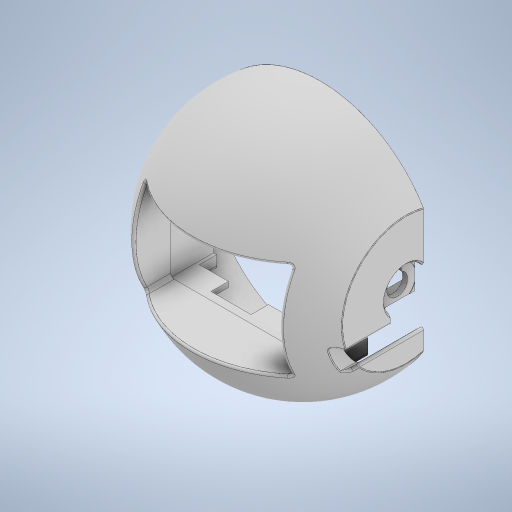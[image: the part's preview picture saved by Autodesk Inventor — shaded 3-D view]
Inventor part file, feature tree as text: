
AUTODESK INVENTOR PART (.ipt)
format: ipt  version: 2023.1 (Build 271208000, 208)  size: 808,448 bytes
history: native  units: mm
features: extrude x28, sketch x27, fillet x7, projected_geometry x5, chamfer x4, other x3, revolve x1, shell x1
ambient origin geometry x8: Origin, YZ Plane, XZ Plane, XY Plane, X Axis, Y Axis, Z Axis, Center Point
bodies: Body1 (feature_tree)
feature tree (76):
  other  "솔리드1"
  sketch  "스케치1"
  revolve  "회전1"
  other  "작업 평면1"
  extrude  "돌출2"  Depth=85.0mm
  other  "작업 평면2"
  extrude  "돌출3"  Depth=56.0mm
  shell  "쉘1"  Thickness=17.0mm
  extrude  "돌출4"  Depth=140.0mm
  extrude  "돌출5"  Depth=4.0mm
  extrude  "돌출6"  TaperAngle=360.0deg  [1 undecoded]
  extrude  "돌출7"  Depth=84.0mm
  extrude  "돌출8"  Depth=55.0mm
  extrude  "돌출9"  Depth=32.0mm TaperAngle=0.0deg
  extrude  "돌출10"  [1 undecoded]
  extrude  "돌출11"  Depth=165.25mm TaperAngle=0.0deg
  extrude  "돌출12"  Depth=4.0mm
  fillet  "모깎기1"  Radius=85.5mm
  extrude  "돌출13"  Depth=57.0mm
  extrude  "돌출14"  Depth=25.5mm TaperAngle=0.0deg
  chamfer  "모따기2"  Distance=17.0mm
  extrude  "돌출16"  Depth=16.5mm
  fillet  "모깎기2"  Radius=10.0mm
  fillet  "모깎기3"  Radius=18.5mm
  fillet  "모깎기4"  Radius=13.0mm
  fillet  "모깎기5"  Radius=12.0mm
  extrude  "돌출17"  Depth=35.25mm TaperAngle=0.0deg
  sketch  "스케치19"
  extrude  "돌출19"  Depth=2.0mm
  extrude  "돌출20"  Depth=16.0mm TaperAngle=0.0deg
  extrude  "돌출21"  Depth=2.0mm
  sketch  "스케치22"
  extrude  "돌출22"  Depth=27.0mm
  extrude  "돌출23"  Depth=9.0mm
  extrude  "돌출24"  Depth=10.0mm TaperAngle=0.0deg
  extrude  "돌출26"  Depth=8.0mm
  extrude  "돌출27"  Depth=23.0mm
  extrude  "돌출28"  Depth=20.0mm TaperAngle=0.0deg
  fillet  "모깎기6"  Radius=10.0mm
  chamfer  "모따기3"  Distance=7.5mm
  extrude  "돌출29"  Depth=50.0mm
  extrude  "돌출30"  Depth=20.0mm TaperAngle=0.0deg
  extrude  "돌출31"  Depth=2.0mm
  extrude  "돌출32"  Depth=5.0mm
  fillet  "모깎기7"  Radius=5.0mm
  chamfer  "모따기6"  Distance=2.5mm
  chamfer  "모따기7"  Distance=12.0mm
  sketch  "스케치2"
  sketch  "스케치3"
  sketch  "스케치5"
  projected_geometry  "투영된 루프1"
  sketch  "스케치6"
  projected_geometry  "투영된 루프2"
  sketch  "스케치7"
  sketch  "스케치8"
  sketch  "스케치9"
  sketch  "스케치10"
  sketch  "스케치11"
  projected_geometry  "투영된 루프3"
  sketch  "스케치12"
  sketch  "스케치13"
  sketch  "스케치15"
  sketch  "스케치16"
  projected_geometry  "투영된 루프4"
  sketch  "스케치17"
  sketch  "스케치18"
  sketch  "스케치20"
  sketch  "스케치21"
  projected_geometry  "투영된 루프5"
  sketch  "스케치23"
  sketch  "스케치24"
  sketch  "스케치25"
  sketch  "스케치26"
  sketch  "스케치27"
  sketch  "스케치29"
  sketch  "스케치30"
note: 2 required parameter values undecoded (feature->parameter linkage not recoverable at this tier; creation-order binding heuristic only, values carry confidence <= 0.55)
